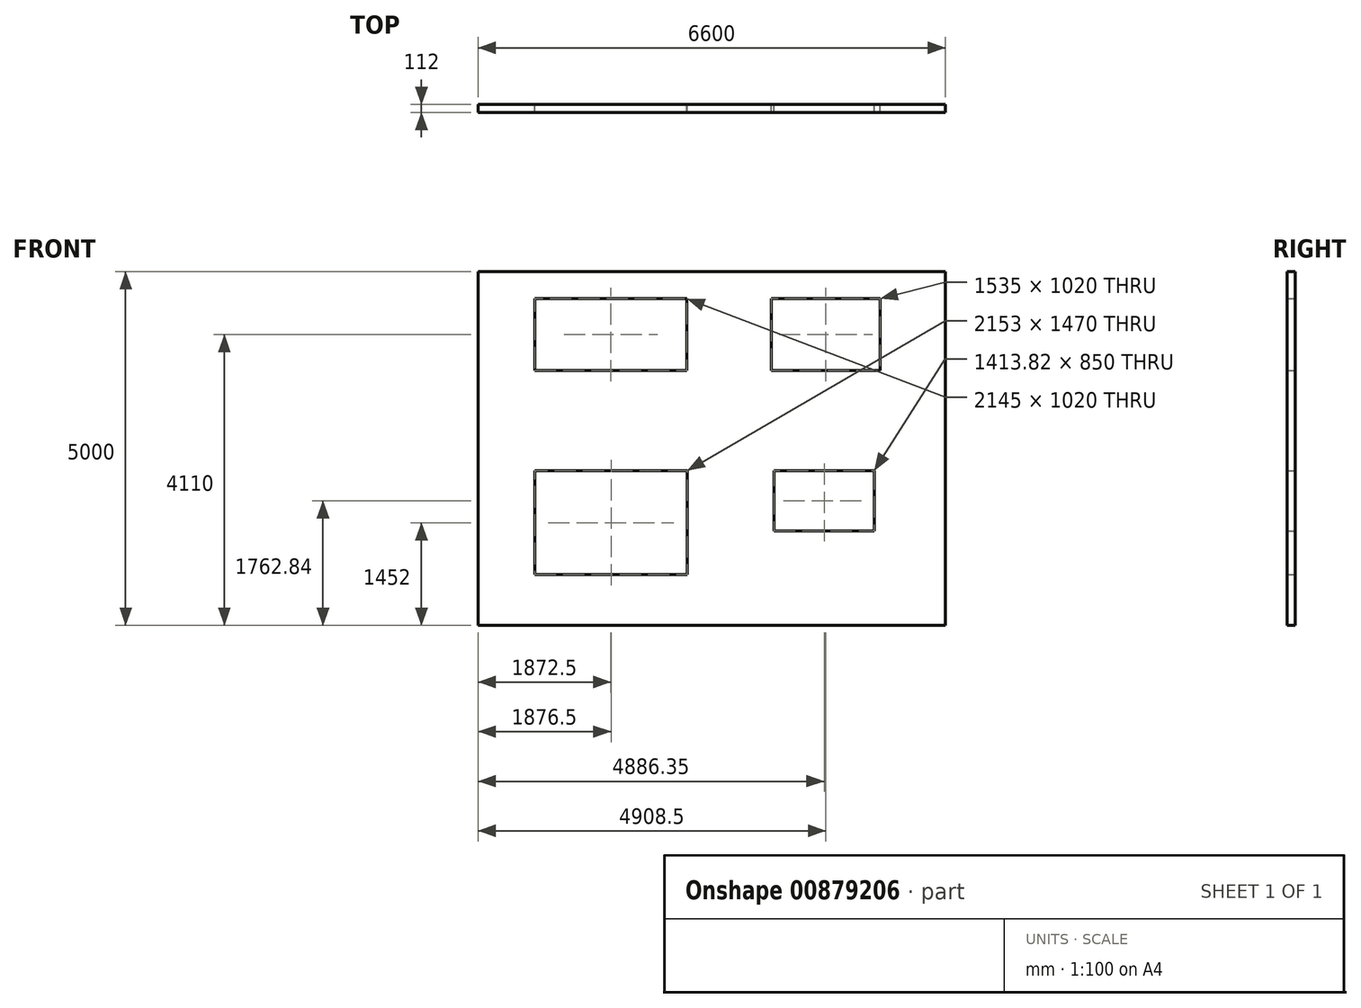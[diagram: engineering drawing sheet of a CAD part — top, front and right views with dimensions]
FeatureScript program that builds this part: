
annotation { "Feature Type Name" : "Feature", "Feature Type Description" : "" }
export const myFeature = defineFeature(function(context is Context, id is Id, definition is map)
    precondition{}
    {
        {
            var Q0;
            Q0=qCreatedBy(makeId("Front.planeOp"),FACE);
            var sketch = newSketch(context, id + "F0", { "sketchPlane" : qUnion([Q0])});
            skLineSegment(sketch, "E0.bottom", {"start": v(3288.8, -2773.48) * mm, "end": v(-3311.2, -2773.48) * mm});
            skLineSegment(sketch, "E0.top", {"start": v(3288.8, 2226.52) * mm, "end": v(-3311.2, 2226.52) * mm});
            skLineSegment(sketch, "E0.left", {"start": v(3288.8, -2773.48) * mm, "end": v(3288.8, 2226.52) * mm});
            skLineSegment(sketch, "E0.right", {"start": v(-3311.2, -2773.48) * mm, "end": v(-3311.2, 2226.52) * mm});
            skLineSegment(sketch, "E1.bottom", {"start": v(-2511.2, 1846.52) * mm, "end": v(-366.2, 1846.52) * mm});
            skLineSegment(sketch, "E1.top", {"start": v(-2511.2, 826.52) * mm, "end": v(-366.2, 826.52) * mm});
            skLineSegment(sketch, "E1.left", {"start": v(-2511.2, 1846.52) * mm, "end": v(-2511.2, 826.52) * mm});
            skLineSegment(sketch, "E1.right", {"start": v(-366.2, 1846.52) * mm, "end": v(-366.2, 826.52) * mm});
            skLineSegment(sketch, "E2.bottom", {"start": v(2364.8, 1846.52) * mm, "end": v(829.8, 1846.52) * mm});
            skLineSegment(sketch, "E2.top", {"start": v(2364.8, 826.52) * mm, "end": v(829.8, 826.52) * mm});
            skLineSegment(sketch, "E2.left", {"start": v(2364.8, 1846.52) * mm, "end": v(2364.8, 826.52) * mm});
            skLineSegment(sketch, "E2.right", {"start": v(829.8, 1846.52) * mm, "end": v(829.8, 826.52) * mm});
            skLineSegment(sketch, "E3.bottom", {"start": v(-2511.2, -2056.48) * mm, "end": v(-358.2, -2056.48) * mm});
            skLineSegment(sketch, "E3.top", {"start": v(-2511.2, -586.48) * mm, "end": v(-358.2, -586.48) * mm});
            skLineSegment(sketch, "E3.left", {"start": v(-2511.2, -2056.48) * mm, "end": v(-2511.2, -586.48) * mm});
            skLineSegment(sketch, "E3.right", {"start": v(-358.2, -2056.48) * mm, "end": v(-358.2, -586.48) * mm});
            skLineSegment(sketch, "E4.bottom", {"start": v(2282.06, -585.64) * mm, "end": v(868.24, -585.64) * mm});
            skLineSegment(sketch, "E4.top", {"start": v(2282.06, -1435.64) * mm, "end": v(868.24, -1435.64) * mm});
            skLineSegment(sketch, "E4.left", {"start": v(2282.06, -585.64) * mm, "end": v(2282.06, -1435.64) * mm});
            skLineSegment(sketch, "E4.right", {"start": v(868.24, -585.64) * mm, "end": v(868.24, -1435.64) * mm});
            skSolve(sketch);
        }
        {
            var Q0;
            Q0=qSketchRegion(id+"F0",true);
            extrude(context, id + "F1", {"entities" : qUnion([Q0]), "depth" : 112 * mm, "offsetDistance" : 25 * mm});
        }
    });
